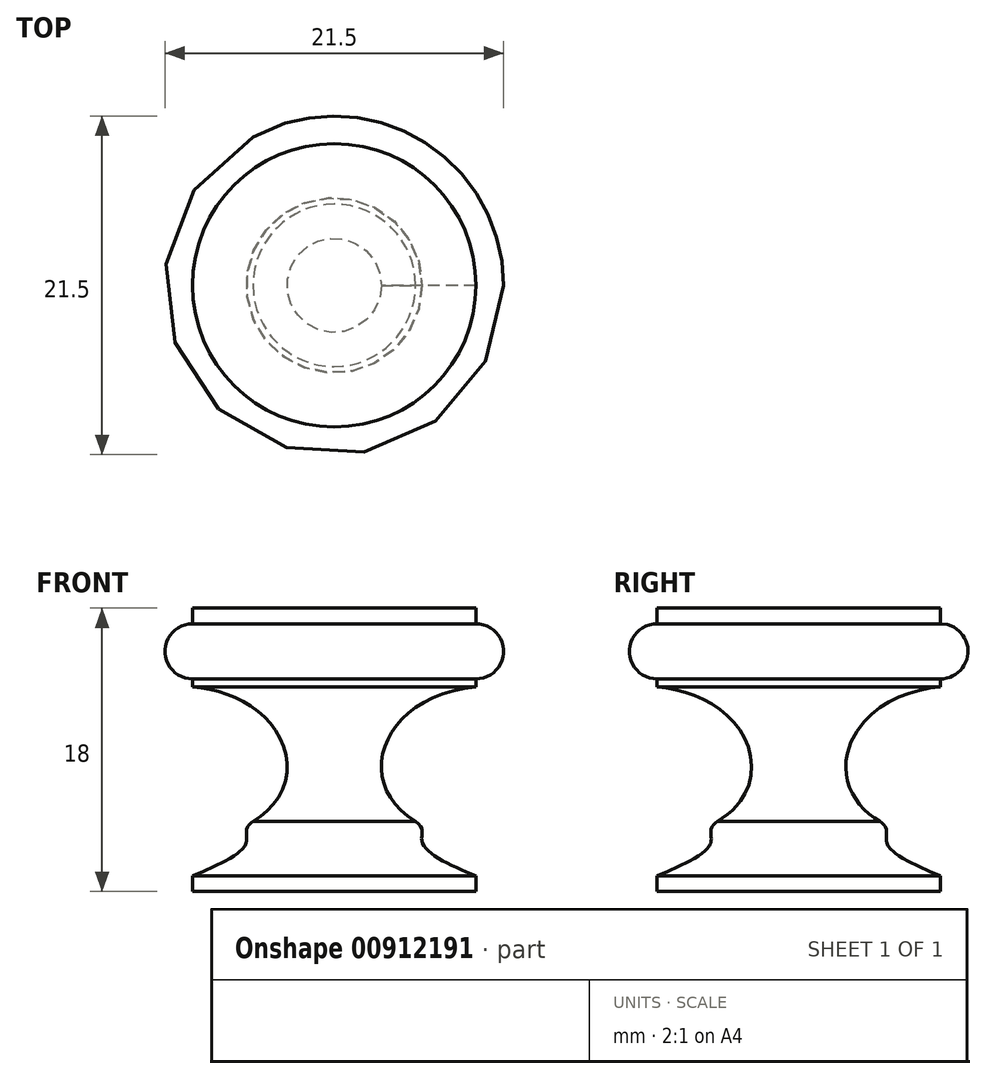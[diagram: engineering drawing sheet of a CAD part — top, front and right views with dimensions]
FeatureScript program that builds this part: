
annotation { "Feature Type Name" : "Feature", "Feature Type Description" : "" }
export const myFeature = defineFeature(function(context is Context, id is Id, definition is map)
    precondition{}
    {
        {
            var Q0;
            Q0=qCreatedBy(makeId("Front.planeOp"),FACE);
            var sketch = newSketch(context, id + "F0", { "sketchPlane" : qUnion([Q0])});
            skLineSegment(sketch, "E0", {"start": v(0, 0) * mm, "end": v(-9, 0) * mm});
            skLineSegment(sketch, "E1", {"start": v(-9, 0) * mm, "end": v(0, 0) * mm});
            skLineSegment(sketch, "E2", {"start": v(0, 18) * mm, "end": v(0, 0) * mm});
            skLineSegment(sketch, "E3", {"start": v(0, 18) * mm, "end": v(-9, 18) * mm});
            skLineSegment(sketch, "E4", {"start": v(-9, 18) * mm, "end": v(-9, 17) * mm});
            skLineSegment(sketch, "E5", {"start": v(-9, 17) * mm, "end": v(-9, 13.5) * mm});
            skLineSegment(sketch, "E6", {"start": v(-9, 13.5) * mm, "end": v(-9, 13) * mm});
            skArc(sketch, "E7", {"start": v(-9, 17) * mm, "mid": v(-10.75, 15.25) * mm, "end": v(-9, 13.5) * mm});
            skLineSegment(sketch, "E8", {"start": v(-9, 0) * mm, "end": v(-9, 1) * mm});
            skFitSpline(sketch, "E9", {"points": [v(-9, 13) * mm, v(-5.16, 4.46) * mm], "startDerivative": vector(17.96, -1.68) * mm, "endDerivative": vector(-12.28, -7.29) * mm});
            skFitSpline(sketch, "E10", {"points": [v(-9, 1) * mm, v(-5.58, 3.1) * mm, v(-5.16, 4.46) * mm], "startDerivative": vector(6.95, 2.78) * mm, "endDerivative": vector(5.65, 3.56) * mm});
            skSolve(sketch);
        }
        {
            var Q0;
            Q0 = qSketchRegion(id + "F0", true);
            var Q1;
            Q1=sQuery(id+"F0.wireOp",EDGE,"E2");
            revolve(context, id + "F1", {"surfaceOperationType" : NewSurfaceOperationType.NEW, "entities" : qUnion([Q0]), "axis" : qUnion([Q1]), "revolveType" : RevolveType.FULL});
        }
    });
